# Revit family: Reductores Velocidad Big-Slow 900x50
name_source: partatom
category: Furniture
units: mm (PartAtom-declared; Revit-internal decimal feet)

## family parameters
Always vertical = Yes
Cut with Voids When Loaded = No
OmniClass Number = 23.40.20.00
OmniClass Title = General Furniture and Specialties
Room Calculation Point = No
Shared = No
Work Plane-Based = No

## types (2) — shared parameters
A = 0.9 m
Fabricante = BENITO URBAN SL
Ficha_Tecnica = https://www.benito.com
H = 0.05 m
Material = 100% reciclable y ecológico
Type Comments = Anclaje recomendado: Mediante tornillos M8 y anclaje plástico. (no subministrados)
URL_Producto = https://www.benito.com
zero-valued in all types: Default Elevation

## per-type parameters (varying)
| type | B | B1 | Description | Referencia |
| Reductores Velocidad Big-Slow 900x50-Cuerpo-VBA15-900mm | 0.5 m | 0 m | Reductor de velocidad de 50 mm de altura para vías públicas con límite de velocidad <50Km/h. | VBA15 |
| Reductores Velocidad Big-Slow 900x50-Borde Macho-VBA15-900mm | 0 m | 0.25 m | Reductor de velocidad de 50 mm de altura para vías públicas con límite de velocidad <50Km/h | VBA14 |

type visibility flags: 2 boolean params named "<type name>" — each type sets only its own to Yes (folded from table)

## geometry (parser evidence)
native form markers: Blend x4, Sweep x8
no freeform markers — native parametric forms only
